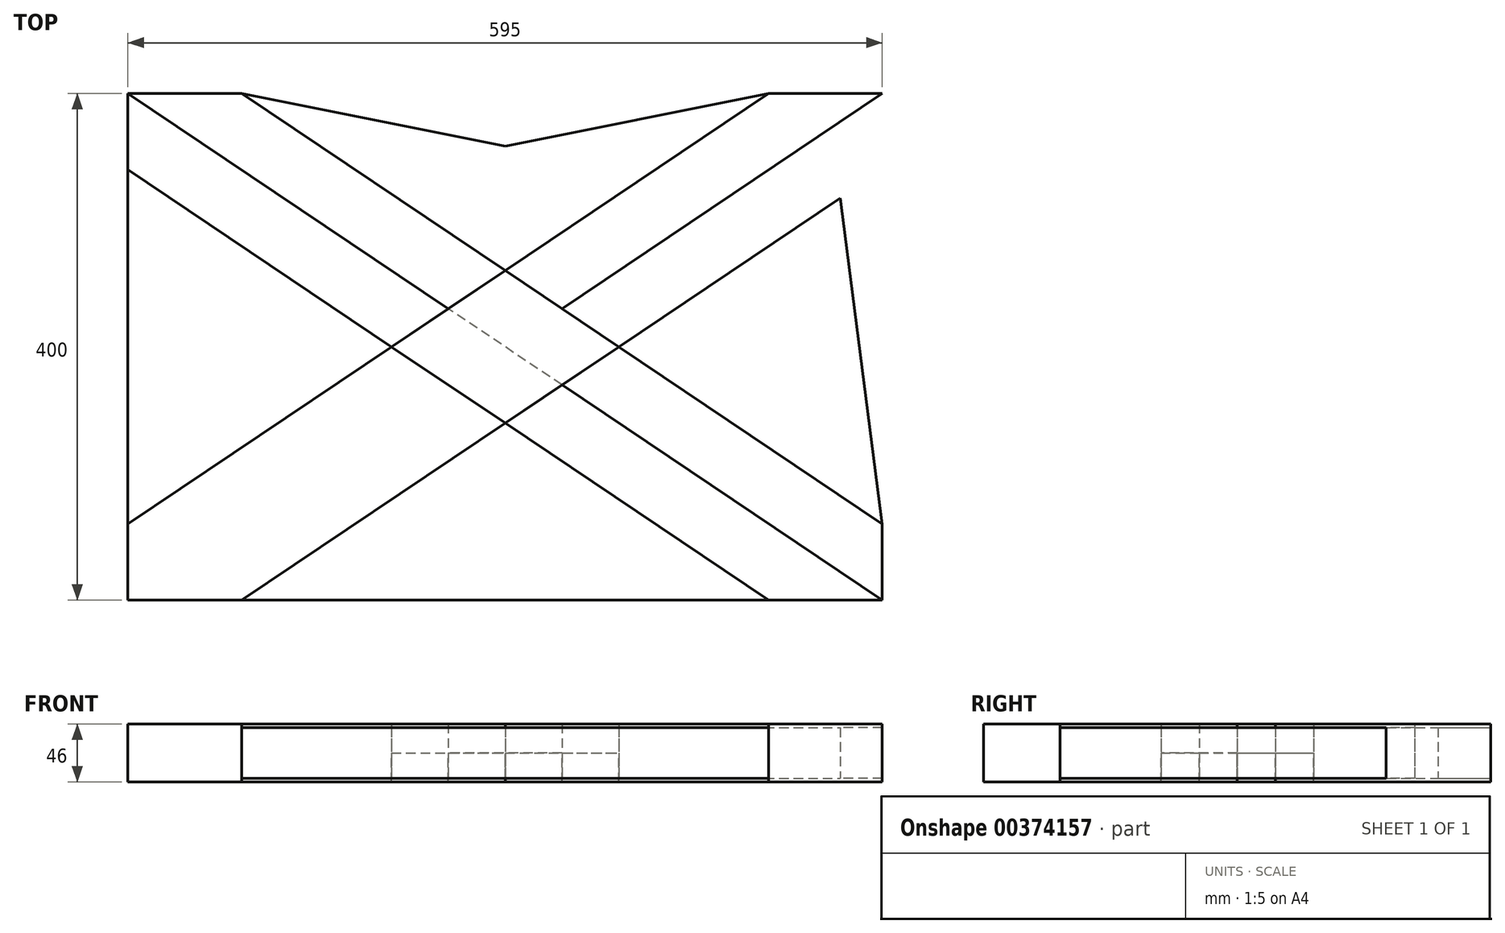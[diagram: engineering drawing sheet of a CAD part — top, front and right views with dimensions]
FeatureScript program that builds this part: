
annotation { "Feature Type Name" : "Feature", "Feature Type Description" : "" }
export const myFeature = defineFeature(function(context is Context, id is Id, definition is map)
    precondition{}
    {
        {
            var Q0;
            Q0=qCreatedBy(makeId("Top.planeOp"),FACE);
            var sketch = newSketch(context, id + "F0", { "sketchPlane" : qUnion([Q0])});
            skLineSegment(sketch, "E0.bottom", {"start": v(297.5, 200) * mm, "end": v(-297.5, 200) * mm});
            skLineSegment(sketch, "E0.top", {"start": v(297.5, -200) * mm, "end": v(-297.5, -200) * mm});
            skLineSegment(sketch, "E0.left", {"start": v(297.5, 200) * mm, "end": v(297.5, -200) * mm});
            skLineSegment(sketch, "E0.right", {"start": v(-297.5, 200) * mm, "end": v(-297.5, -200) * mm});
            skPoint(sketch, "E0.middle", {"position": v(0, 0) * mm});
            skLineSegment(sketch, "E1", {"start": v(297.5, -200) * mm, "end": v(-297.5, 200) * mm});
            skLineSegment(sketch, "E2", {"start": v(-297.5, 139.75) * mm, "end": v(207.88, -200) * mm});
            skLineSegment(sketch, "E3", {"start": v(297.5, -139.75) * mm, "end": v(-207.88, 200) * mm});
            skLineSegment(sketch, "E4", {"start": v(-297.5, -200) * mm, "end": v(297.5, 200) * mm});
            skLineSegment(sketch, "E5", {"start": v(-297.5, -139.75) * mm, "end": v(207.88, 200) * mm});
            skLineSegment(sketch, "E6", {"start": v(-207.88, -200) * mm, "end": v(297.5, 139.75) * mm});
            skLineSegment(sketch, "E7", {"start": v(-207.88, 200) * mm, "end": v(0, 158.3) * mm});
            skLineSegment(sketch, "E8", {"start": v(0, 158.3) * mm, "end": v(207.88, 200) * mm});
            skLineSegment(sketch, "E9", {"start": v(297.5, 139.75) * mm, "end": v(264.3, 117.44) * mm});
            skLineSegment(sketch, "E10", {"start": v(297.5, -139.75) * mm, "end": v(264.3, 117.44) * mm});
            skSolve(sketch);
        }
        {
            var Q0;
            {var subQ1=sQuery(id+"F0.wireOp",EDGE,"E0.top");var subQ3=sQuery(id+"F0.wireOp",EDGE,"E2");var subQ4=makeQuery(id+"F0.imprint","INTERSECT",VERTEX,{"derivedFrom":[subQ1,subQ3]});Q0=makeQuery(id+"F0.imprint","IMPRINT",FACE,{"disambiguationData":[TD([[makeQuery(id+"F0.imprint","IMPRINT",EDGE,{"disambiguationData":[TD([[subQ4,1.0]])],"derivedFrom":subQ3}),1.0]])]});}
            var Q1;
            {var subQ1=sQuery(id+"F0.wireOp",EDGE,"E0.right");var subQ3=sQuery(id+"F0.wireOp",EDGE,"E2");var subQ4=makeQuery(id+"F0.imprint","INTERSECT",VERTEX,{"derivedFrom":[subQ1,subQ3]});Q1=makeQuery(id+"F0.imprint","IMPRINT",FACE,{"disambiguationData":[TD([[makeQuery(id+"F0.imprint","IMPRINT",EDGE,{"disambiguationData":[TD([[subQ4,-1.0]])],"derivedFrom":subQ3}),1.0]])]});}
            extrude(context, id + "F1", {"entities" : qUnion([Q0, Q1]), "endBound" : BoundingType.SYMMETRIC, "depth" : 46 * mm});
        }
        {
            var Q0;
            {var subQ0=sQuery(id+"F0.wireOp",EDGE,"E6");var subQ1=sQuery(id+"F0.wireOp",EDGE,"E1");var subQ2=makeQuery(id+"F0.imprint","INTERSECT",VERTEX,{"derivedFrom":[subQ1,subQ0]});Q0=makeQuery(id+"F0.imprint","IMPRINT",FACE,{"disambiguationData":[TD([[makeQuery(id+"F0.imprint","IMPRINT",EDGE,{"disambiguationData":[TD([[subQ2,-1.0]])],"derivedFrom":subQ1}),1.0]])]});}
            var Q1;
            {var subQ0=sQuery(id+"F0.wireOp",EDGE,"E4");var subQ1=sQuery(id+"F0.wireOp",EDGE,"E1");var subQ2=makeQuery(id+"F0.imprint","INTERSECT",VERTEX,{"derivedFrom":[subQ1,subQ0]});Q1=makeQuery(id+"F0.imprint","IMPRINT",FACE,{"disambiguationData":[TD([[makeQuery(id+"F0.imprint","IMPRINT",EDGE,{"disambiguationData":[TD([[subQ2,-1.0]])],"derivedFrom":subQ1}),1.0]])]});}
            extrude(context, id + "F2", {"entities" : qUnion([Q0, Q1]), "oppositeDirection" : true, "depth" : 23 * mm});
        }
        {
            var Q0;
            {var subQ0=sQuery(id+"F0.wireOp",EDGE,"E1");var subQ5=sQuery(id+"F0.wireOp",EDGE,"E5");var subQ6=makeQuery(id+"F0.imprint","INTERSECT",VERTEX,{"derivedFrom":[subQ0,subQ5]});Q0=makeQuery(id+"F0.imprint","IMPRINT",FACE,{"disambiguationData":[TD([[makeQuery(id+"F0.imprint","IMPRINT",EDGE,{"disambiguationData":[TD([[subQ6,-1.0]])],"derivedFrom":subQ5}),1.0]])]});}
            var Q1;
            {var subQ0=sQuery(id+"F0.wireOp",EDGE,"E1");var subQ5=sQuery(id+"F0.wireOp",EDGE,"E6");var subQ6=makeQuery(id+"F0.imprint","INTERSECT",VERTEX,{"derivedFrom":[subQ0,subQ5]});Q1=makeQuery(id+"F0.imprint","IMPRINT",FACE,{"disambiguationData":[TD([[makeQuery(id+"F0.imprint","IMPRINT",EDGE,{"disambiguationData":[TD([[subQ6,-1.0]])],"derivedFrom":subQ5}),-1.0]])]});}
            extrude(context, id + "F3", {"entities" : qUnion([Q0, Q1]), "endBound" : BoundingType.SYMMETRIC, "depth" : 46 * mm});
        }
        {
            var Q0;
            {var subQ0=sQuery(id+"F0.wireOp",EDGE,"E6");var subQ1=sQuery(id+"F0.wireOp",EDGE,"E1");var subQ2=makeQuery(id+"F0.imprint","INTERSECT",VERTEX,{"derivedFrom":[subQ1,subQ0]});Q0=makeQuery(id+"F0.imprint","IMPRINT",FACE,{"disambiguationData":[TD([[makeQuery(id+"F0.imprint","IMPRINT",EDGE,{"disambiguationData":[TD([[subQ2,-1.0]])],"derivedFrom":subQ1}),-1.0]])]});}
            var Q1;
            {var subQ0=sQuery(id+"F0.wireOp",EDGE,"E4");var subQ1=sQuery(id+"F0.wireOp",EDGE,"E1");var subQ2=makeQuery(id+"F0.imprint","INTERSECT",VERTEX,{"derivedFrom":[subQ1,subQ0]});Q1=makeQuery(id+"F0.imprint","IMPRINT",FACE,{"disambiguationData":[TD([[makeQuery(id+"F0.imprint","IMPRINT",EDGE,{"disambiguationData":[TD([[subQ2,-1.0]])],"derivedFrom":subQ1}),-1.0]])]});}
            extrude(context, id + "F4", {"entities" : qUnion([Q0, Q1]), "depth" : -23 * mm});
        }
        {
            var Q0;
            {var subQ0=sQuery(id+"F0.wireOp",EDGE,"E4");var subQ5=sQuery(id+"F0.wireOp",EDGE,"E2");var subQ6=makeQuery(id+"F0.imprint","INTERSECT",VERTEX,{"derivedFrom":[subQ5,subQ0]});Q0=makeQuery(id+"F0.imprint","IMPRINT",FACE,{"disambiguationData":[TD([[makeQuery(id+"F0.imprint","IMPRINT",EDGE,{"disambiguationData":[TD([[subQ6,-1.0]])],"derivedFrom":subQ5}),-1.0]])]});}
            var Q1;
            {var subQ3=sQuery(id+"F0.wireOp",EDGE,"E5");var subQ5=sQuery(id+"F0.wireOp",EDGE,"E2");var subQ6=makeQuery(id+"F0.imprint","INTERSECT",VERTEX,{"derivedFrom":[subQ5,subQ3]});Q1=makeQuery(id+"F0.imprint","IMPRINT",FACE,{"disambiguationData":[TD([[makeQuery(id+"F0.imprint","IMPRINT",EDGE,{"disambiguationData":[TD([[subQ6,-1.0]])],"derivedFrom":subQ5}),-1.0]])]});}
            var Q2;
            {var subQ0=sQuery(id+"F0.wireOp",EDGE,"E9");Q2=makeQuery(id+"F0.imprint","IMPRINT",FACE,{"disambiguationData":[TD([[makeQuery(id+"F0.imprint","IMPRINT",EDGE,{"derivedFrom":subQ0}),-1.0]])]});}
            var Q3;
            {var subQ0=sQuery(id+"F0.wireOp",EDGE,"E4");var subQ5=sQuery(id+"F0.wireOp",EDGE,"E3");var subQ6=makeQuery(id+"F0.imprint","INTERSECT",VERTEX,{"derivedFrom":[subQ5,subQ0]});Q3=makeQuery(id+"F0.imprint","IMPRINT",FACE,{"disambiguationData":[TD([[makeQuery(id+"F0.imprint","IMPRINT",EDGE,{"disambiguationData":[TD([[subQ6,-1.0]])],"derivedFrom":subQ5}),-1.0]])]});}
            extrude(context, id + "F5", {"entities" : qUnion([Q0, Q1, Q2, Q3]), "endBound" : BoundingType.SYMMETRIC, "depth" : 46 * mm});
        }
        {
            var Q0;
            {var subQ0=sQuery(id+"F0.wireOp",EDGE,"E6");var subQ1=sQuery(id+"F0.wireOp",EDGE,"E1");var subQ2=makeQuery(id+"F0.imprint","INTERSECT",VERTEX,{"derivedFrom":[subQ1,subQ0]});Q0=makeQuery(id+"F0.imprint","IMPRINT",FACE,{"disambiguationData":[TD([[makeQuery(id+"F0.imprint","IMPRINT",EDGE,{"disambiguationData":[TD([[subQ2,-1.0]])],"derivedFrom":subQ1}),-1.0]])]});}
            var Q1;
            {var subQ0=sQuery(id+"F0.wireOp",EDGE,"E4");var subQ1=sQuery(id+"F0.wireOp",EDGE,"E1");var subQ2=makeQuery(id+"F0.imprint","INTERSECT",VERTEX,{"derivedFrom":[subQ1,subQ0]});Q1=makeQuery(id+"F0.imprint","IMPRINT",FACE,{"disambiguationData":[TD([[makeQuery(id+"F0.imprint","IMPRINT",EDGE,{"disambiguationData":[TD([[subQ2,-1.0]])],"derivedFrom":subQ1}),-1.0]])]});}
            var Q2;
            {var subQ0=sQuery(id+"F0.wireOp",EDGE,"E4");var subQ1=sQuery(id+"F0.wireOp",EDGE,"E1");var subQ2=makeQuery(id+"F0.imprint","INTERSECT",VERTEX,{"derivedFrom":[subQ1,subQ0]});Q2=makeQuery(id+"F0.imprint","IMPRINT",FACE,{"disambiguationData":[TD([[makeQuery(id+"F0.imprint","IMPRINT",EDGE,{"disambiguationData":[TD([[subQ2,-1.0]])],"derivedFrom":subQ1}),1.0]])]});}
            var Q3;
            {var subQ0=sQuery(id+"F0.wireOp",EDGE,"E6");var subQ1=sQuery(id+"F0.wireOp",EDGE,"E1");var subQ2=makeQuery(id+"F0.imprint","INTERSECT",VERTEX,{"derivedFrom":[subQ1,subQ0]});Q3=makeQuery(id+"F0.imprint","IMPRINT",FACE,{"disambiguationData":[TD([[makeQuery(id+"F0.imprint","IMPRINT",EDGE,{"disambiguationData":[TD([[subQ2,-1.0]])],"derivedFrom":subQ1}),1.0]])]});}
            extrude(context, id + "F6", {"entities" : qUnion([Q0, Q1, Q2, Q3]), "depth" : 23 * mm});
        }
        {
            var Q0;
            {var subQ0=sQuery(id+"F0.wireOp",EDGE,"E2");var subQ1=sQuery(id+"F0.wireOp",EDGE,"E0.right");var subQ2=makeQuery(id+"F0.imprint","INTERSECT",VERTEX,{"derivedFrom":[subQ1,subQ0]});Q0=makeQuery(id+"F0.imprint","IMPRINT",FACE,{"disambiguationData":[TD([[makeQuery(id+"F0.imprint","IMPRINT",EDGE,{"disambiguationData":[TD([[subQ2,-1.0]])],"derivedFrom":subQ1}),1.0]])]});}
            var Q1;
            {var subQ0=sQuery(id+"F0.wireOp",EDGE,"E2");var subQ1=sQuery(id+"F0.wireOp",EDGE,"E0.top");var subQ2=makeQuery(id+"F0.imprint","INTERSECT",VERTEX,{"derivedFrom":[subQ1,subQ0]});Q1=makeQuery(id+"F0.imprint","IMPRINT",FACE,{"disambiguationData":[TD([[makeQuery(id+"F0.imprint","IMPRINT",EDGE,{"disambiguationData":[TD([[subQ2,-1.0]])],"derivedFrom":subQ1}),-1.0]])]});}
            var Q2;
            {var subQ0=sQuery(id+"F0.wireOp",EDGE,"E10");Q2=makeQuery(id+"F0.imprint","IMPRINT",FACE,{"disambiguationData":[TD([[makeQuery(id+"F0.imprint","IMPRINT",EDGE,{"derivedFrom":subQ0}),1.0]])]});}
            var Q3;
            {var subQ0=sQuery(id+"F0.wireOp",EDGE,"E7");Q3=makeQuery(id+"F0.imprint","IMPRINT",FACE,{"disambiguationData":[TD([[makeQuery(id+"F0.imprint","IMPRINT",EDGE,{"derivedFrom":subQ0}),-1.0]])]});}
            extrude(context, id + "F7", {"entities" : qUnion([Q0, Q1, Q2, Q3]), "endBound" : BoundingType.SYMMETRIC, "depth" : 40 * mm});
        }
    });
